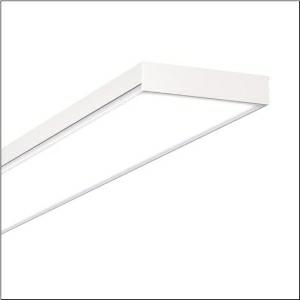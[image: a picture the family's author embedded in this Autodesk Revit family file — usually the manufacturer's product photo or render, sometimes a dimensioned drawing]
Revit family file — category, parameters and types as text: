
# Revit family: apollon_r__31_surface_51mp26wm2341w_1193
name_source: partatom
category: Lighting Fixtures
units: mm (PartAtom-declared; Revit-internal decimal feet)

## family parameters
Cut with Voids When Loaded = No
Host = Face
Light Source = No
Part Type = Normal
Room Calculation Point = No
Round Connector Dimension = Use Diameter
Shared = No

## types (1)
- Apollon® 31 Surface (1 x LED, 4400 lm, 33 W, 3000K)
    Apparent Load = 33 VA
    CIE Flux Codes = 61 87 97 97 100
    Color Rendering = 80
    Color Temperature = 3000K
    Default Elevation = 1800 mm
    Description = Apollon® 31 Surface, office luminaire, primary optical cover: micro prismatic cover, of PMMA, light emission: direct distribution, primary light characteristic: symmetric, installation type: surface-mounted, LED, rated luminous flux: 4.400lm, luminous efficacy: 133lm/W, light colour: 830, colour temperature: 3000K, control gear: ON/OFF Multilumen, with terminal, 3-pole, mains connection: 220..240V, AC, 50/60Hz, rated input power: 33W, housing, of sheet steel, coil coated, traffic white (RAL 9016), length: 1.545mm, width: 200mm, height: 44mm, protection rating (complete): IP20, insulation class (complete): insulation class II (safety insulation), certification: CE, impact resistance: IK02, permissible operating ambient temperature: -20..+40°C, packaging unit: 1 piece
    Height = 44 mm
    Lamp = 1 x LED
    Lamp Light Flux = 4400 lm
    Lamp Power = 33 W
    Lamp count = 1
    Length = 1545 mm
    Luminous efficacy = 133 lm/W
    Manufacturer = Siteco
    ModVariant = No
    Model = 51MP26WM2341W
    Mounting Place = Ceiling
    Mounting Type = Surface mounted
    Number of Poles = 1
    OnlyDefault = Yes
    Power Factor = 1
    Product Name = Apollon® 31 Surface
    Product group = office luminaire | ceiling mounted
    ProductGroupID = 302
    Protection Class = Protection class II
    Protection Degree = IP 20
    RLX_Detail_Level = 1
    RLX_Emergency_Light_Flux = 0 lm
    RLX_Emergency_Type = 0
    RLX_Emergency_Type_DB = No
    RlxData = <blob elided: 20757 chars, md5=2d8bddc4>
    Socket = socket
    Standby Power = 0 W
    System Light Flux = 4400 lm
    System Power = 33 W
    Type Comments = Product without accessories
    Type Image = l_1313658.jpg
    URL = http://relux.com
    VarID = ---
    Voltage = 0 V
    Weight = 0.00 kg
    Width = 200 mm  [stored 0.656168 ft]

note: [stored X ft] marks values corroborated as IEEE doubles in the binary element streams (Revit-internal decimal feet)

## geometry (parser evidence)
native form markers: Blend x4, Sweep x10
no freeform markers — native parametric forms only
